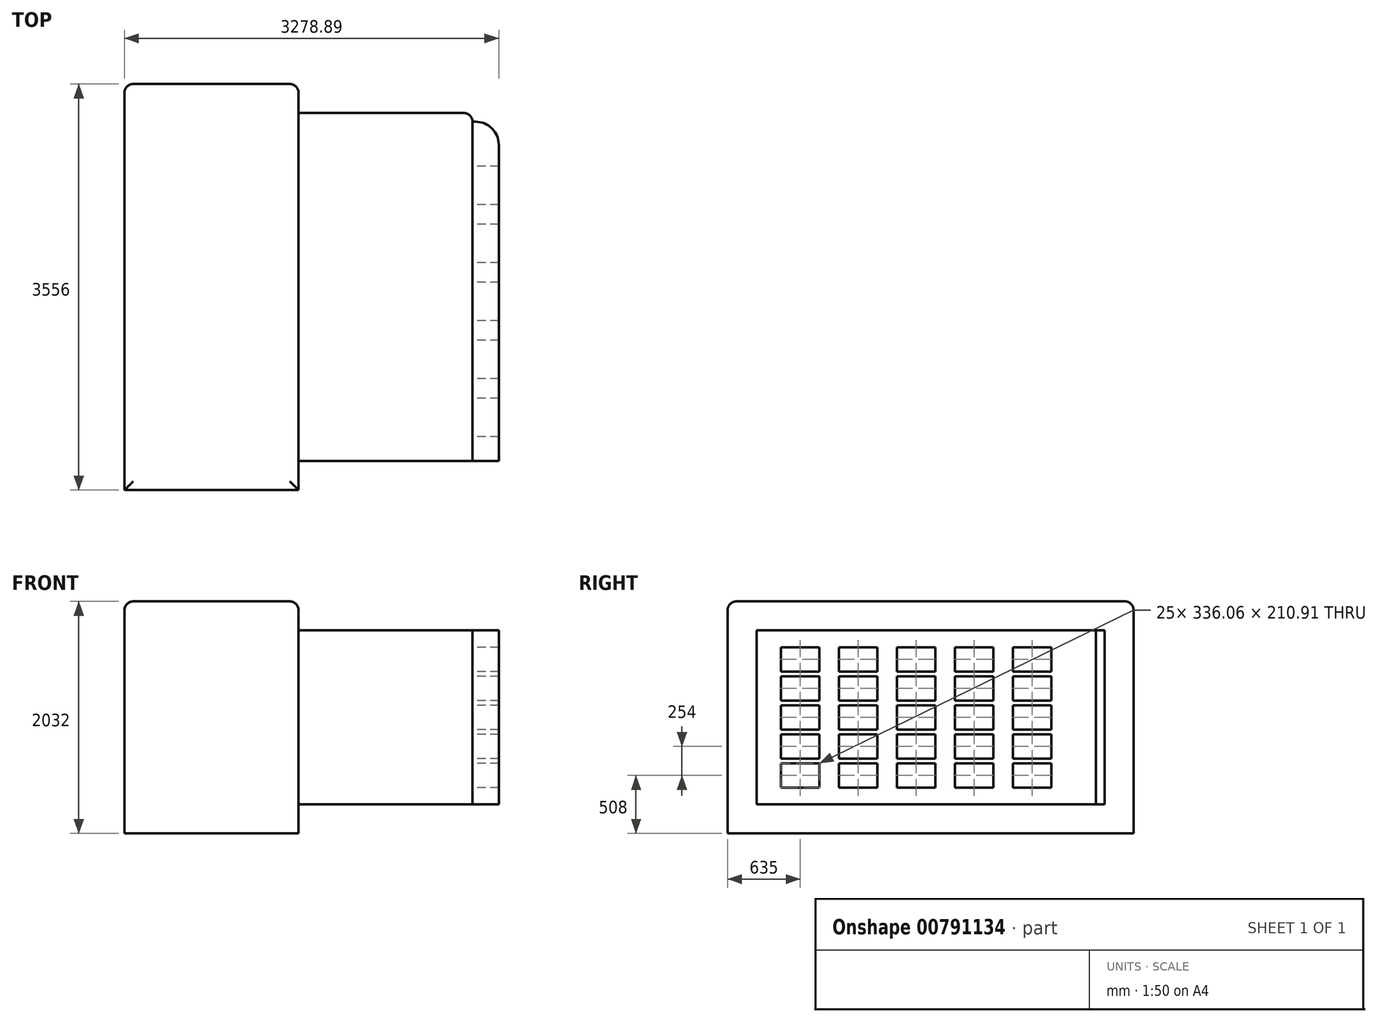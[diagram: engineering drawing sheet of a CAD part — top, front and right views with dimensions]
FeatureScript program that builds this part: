
annotation { "Feature Type Name" : "Feature", "Feature Type Description" : "" }
export const myFeature = defineFeature(function(context is Context, id is Id, definition is map)
    precondition{}
    {
        {
            var Q0;
            Q0=qCreatedBy(makeId("Top.planeOp"),FACE);
            var sketch = newSketch(context, id + "F0", { "sketchPlane" : qUnion([Q0])});
            skLineSegment(sketch, "E0.bottom", {"start": v(1524, -1524) * mm, "end": v(-1524, -1524) * mm});
            skLineSegment(sketch, "E0.top", {"start": v(1524, 1524) * mm, "end": v(-1524, 1524) * mm});
            skLineSegment(sketch, "E0.left", {"start": v(1524, -1524) * mm, "end": v(1524, 1524) * mm});
            skLineSegment(sketch, "E0.right", {"start": v(-1524, -1524) * mm, "end": v(-1524, 1524) * mm});
            skPoint(sketch, "E0.middle", {"position": v(0, 0) * mm});
            skSolve(sketch);
        }
        {
            var Q0;
            Q0 = qSketchRegion(id + "F0", true);
            extrude(context, id + "F1", {"entities" : qUnion([Q0]), "depth" : 1524 * mm, "offsetDistance" : 25.4 * mm});
        }
        {
            var Q0;
            Q0=makeQuery(id+"F1.opExtrude","SWEPT_FACE",FACE,{"disambiguationData":[OSD([sQuery(id+"F0.wireOp",EDGE,"E0.right")])]});
            var sketch = newSketch(context, id + "F2", { "sketchPlane" : qUnion([Q0])});
            skLineSegment(sketch, "E1.0", {"start": v(1524, 1524) * mm, "end": v(-1524, 1524) * mm});
            skLineSegment(sketch, "E2.0", {"start": v(1524, 1524) * mm, "end": v(1524, 0) * mm});
            skLineSegment(sketch, "E3.0", {"start": v(1524, 0) * mm, "end": v(-1524, 0) * mm});
            skLineSegment(sketch, "E4.0", {"start": v(-1524, 1524) * mm, "end": v(-1524, 0) * mm});
            skLineSegment(sketch, "E5.0", {"start": v(1778, 1778) * mm, "end": v(-1778, 1778) * mm});
            skLineSegment(sketch, "E5.1", {"start": v(1778, 1778) * mm, "end": v(1778, -254) * mm});
            skLineSegment(sketch, "E5.2", {"start": v(1778, -254) * mm, "end": v(-1778, -254) * mm});
            skLineSegment(sketch, "E5.3", {"start": v(-1778, 1778) * mm, "end": v(-1778, -254) * mm});
            skSolve(sketch);
        }
        {
            var Q0;
            Q0 = qSketchRegion(id + "F2", true);
            extrude(context, id + "F3", {"entities" : qUnion([Q0]), "operationType" : NewBodyOperationType.ADD, "oppositeDirection" : true, "depth" : 1524 * mm, "offsetDistance" : 25.4 * mm});
        }
        {
            var Q0;
            Q0=makeQuery(id+"F1.opExtrude","SWEPT_EDGE",EDGE,{"disambiguationData":[OSD([sQuery(id+"F0.wireOp",EDGE,"E0.top"),sQuery(id+"F0.wireOp",EDGE,"E0.left")])]});
            var Q1;
            Q1=makeQuery(id+"F3.opExtrude","CAP_EDGE",EDGE,{"disambiguationData":[OSD([sQuery(id+"F2.wireOp",EDGE,"E4.0")])],"isStart":false});
            var Q2;
            Q2=makeQuery(id+"F3.opExtrude","CAP_EDGE",EDGE,{"disambiguationData":[OSD([sQuery(id+"F2.wireOp",EDGE,"E5.3")])],"isStart":false});
            var Q3;
            Q3=makeQuery(id+"F3.opExtrude","CAP_EDGE",EDGE,{"disambiguationData":[OSD([sQuery(id+"F2.wireOp",EDGE,"E5.3")])],"isStart":true});
            var Q4;
            Q4=makeQuery(id+"F3.opExtrude","CAP_EDGE",EDGE,{"disambiguationData":[OSD([sQuery(id+"F2.wireOp",EDGE,"E5.0")])],"isStart":false});
            var Q5;
            Q5=makeQuery(id+"F3.opExtrude","CAP_EDGE",EDGE,{"disambiguationData":[OSD([sQuery(id+"F2.wireOp",EDGE,"E1.0")])],"isStart":false});
            var Q6;
            Q6=makeQuery(id+"F3.opExtrude","SWEPT_FACE",FACE,{"disambiguationData":[OSD([sQuery(id+"F2.wireOp",EDGE,"E5.0")])]});
            fillet(context, id + "F4", {"entities" : qUnion([Q0, Q1, Q2, Q3, Q4, Q5, Q6]), "radius" : 76.2 * mm, "tangentPropagation" : true, "allowEdgeOverflow" : false});
        }
        {
            var Q0;
            Q0=makeQuery(id+"F1.opExtrude","SWEPT_FACE",FACE,{"disambiguationData":[OSD([sQuery(id+"F0.wireOp",EDGE,"E0.left")])]});
            var sketch = newSketch(context, id + "F5", { "sketchPlane" : qUnion([Q0])});
            skLineSegment(sketch, "E6.0", {"start": v(1447.8, 0) * mm, "end": v(1447.8, 1524) * mm});
            skLineSegment(sketch, "E7.0", {"start": v(-1524, 1524) * mm, "end": v(1447.8, 1524) * mm});
            skLineSegment(sketch, "E8.0", {"start": v(-1524, 1524) * mm, "end": v(-1524, 0) * mm});
            skLineSegment(sketch, "E9.0", {"start": v(-1524, 0) * mm, "end": v(1447.8, 0) * mm});
            skLineSegment(sketch, "E10.bottom", {"start": v(-974.97, 359.46) * mm, "end": v(-1311.03, 359.46) * mm});
            skLineSegment(sketch, "E10.top", {"start": v(-974.97, 148.54) * mm, "end": v(-1311.03, 148.54) * mm});
            skLineSegment(sketch, "E10.left", {"start": v(-974.97, 359.46) * mm, "end": v(-974.97, 148.54) * mm});
            skLineSegment(sketch, "E10.right", {"start": v(-1311.03, 359.46) * mm, "end": v(-1311.03, 148.54) * mm});
            skPoint(sketch, "E10.middle", {"position": v(-1143, 254) * mm});
            skLineSegment(sketch, "E11.0.1.0", {"start": v(-1311.03, 613.46) * mm, "end": v(-1311.03, 402.54) * mm});
            skLineSegment(sketch, "E11.0.1.1", {"start": v(-974.97, 613.46) * mm, "end": v(-1311.03, 613.46) * mm});
            skLineSegment(sketch, "E11.0.1.2", {"start": v(-974.97, 613.46) * mm, "end": v(-974.97, 402.54) * mm});
            skLineSegment(sketch, "E11.0.1.3", {"start": v(-974.97, 402.54) * mm, "end": v(-1311.03, 402.54) * mm});
            skLineSegment(sketch, "E11.0.2.0", {"start": v(-1311.03, 867.46) * mm, "end": v(-1311.03, 656.54) * mm});
            skLineSegment(sketch, "E11.0.2.1", {"start": v(-974.97, 867.46) * mm, "end": v(-1311.03, 867.46) * mm});
            skLineSegment(sketch, "E11.0.2.2", {"start": v(-974.97, 867.46) * mm, "end": v(-974.97, 656.54) * mm});
            skLineSegment(sketch, "E11.0.2.3", {"start": v(-974.97, 656.54) * mm, "end": v(-1311.03, 656.54) * mm});
            skLineSegment(sketch, "E11.0.3.0", {"start": v(-1311.03, 1121.46) * mm, "end": v(-1311.03, 910.54) * mm});
            skLineSegment(sketch, "E11.0.3.1", {"start": v(-974.97, 1121.46) * mm, "end": v(-1311.03, 1121.46) * mm});
            skLineSegment(sketch, "E11.0.3.2", {"start": v(-974.97, 1121.46) * mm, "end": v(-974.97, 910.54) * mm});
            skLineSegment(sketch, "E11.0.3.3", {"start": v(-974.97, 910.54) * mm, "end": v(-1311.03, 910.54) * mm});
            skLineSegment(sketch, "E11.0.4.0", {"start": v(-1311.03, 1375.46) * mm, "end": v(-1311.03, 1164.54) * mm});
            skLineSegment(sketch, "E11.0.4.1", {"start": v(-974.97, 1375.46) * mm, "end": v(-1311.03, 1375.46) * mm});
            skLineSegment(sketch, "E11.0.4.2", {"start": v(-974.97, 1375.46) * mm, "end": v(-974.97, 1164.54) * mm});
            skLineSegment(sketch, "E11.0.4.3", {"start": v(-974.97, 1164.54) * mm, "end": v(-1311.03, 1164.54) * mm});
            skLineSegment(sketch, "E11.1.0.0", {"start": v(-803.03, 359.46) * mm, "end": v(-803.03, 148.54) * mm});
            skLineSegment(sketch, "E11.1.0.1", {"start": v(-466.97, 359.46) * mm, "end": v(-803.03, 359.46) * mm});
            skLineSegment(sketch, "E11.1.0.2", {"start": v(-466.97, 359.46) * mm, "end": v(-466.97, 148.54) * mm});
            skLineSegment(sketch, "E11.1.0.3", {"start": v(-466.97, 148.54) * mm, "end": v(-803.03, 148.54) * mm});
            skLineSegment(sketch, "E11.1.1.0", {"start": v(-803.03, 613.46) * mm, "end": v(-803.03, 402.54) * mm});
            skLineSegment(sketch, "E11.1.1.1", {"start": v(-466.97, 613.46) * mm, "end": v(-803.03, 613.46) * mm});
            skLineSegment(sketch, "E11.1.1.2", {"start": v(-466.97, 613.46) * mm, "end": v(-466.97, 402.54) * mm});
            skLineSegment(sketch, "E11.1.1.3", {"start": v(-466.97, 402.54) * mm, "end": v(-803.03, 402.54) * mm});
            skLineSegment(sketch, "E11.1.2.0", {"start": v(-803.03, 867.46) * mm, "end": v(-803.03, 656.54) * mm});
            skLineSegment(sketch, "E11.1.2.1", {"start": v(-466.97, 867.46) * mm, "end": v(-803.03, 867.46) * mm});
            skLineSegment(sketch, "E11.1.2.2", {"start": v(-466.97, 867.46) * mm, "end": v(-466.97, 656.54) * mm});
            skLineSegment(sketch, "E11.1.2.3", {"start": v(-466.97, 656.54) * mm, "end": v(-803.03, 656.54) * mm});
            skLineSegment(sketch, "E11.1.3.0", {"start": v(-803.03, 1121.46) * mm, "end": v(-803.03, 910.54) * mm});
            skLineSegment(sketch, "E11.1.3.1", {"start": v(-466.97, 1121.46) * mm, "end": v(-803.03, 1121.46) * mm});
            skLineSegment(sketch, "E11.1.3.2", {"start": v(-466.97, 1121.46) * mm, "end": v(-466.97, 910.54) * mm});
            skLineSegment(sketch, "E11.1.3.3", {"start": v(-466.97, 910.54) * mm, "end": v(-803.03, 910.54) * mm});
            skLineSegment(sketch, "E11.1.4.0", {"start": v(-803.03, 1375.46) * mm, "end": v(-803.03, 1164.54) * mm});
            skLineSegment(sketch, "E11.1.4.1", {"start": v(-466.97, 1375.46) * mm, "end": v(-803.03, 1375.46) * mm});
            skLineSegment(sketch, "E11.1.4.2", {"start": v(-466.97, 1375.46) * mm, "end": v(-466.97, 1164.54) * mm});
            skLineSegment(sketch, "E11.1.4.3", {"start": v(-466.97, 1164.54) * mm, "end": v(-803.03, 1164.54) * mm});
            skLineSegment(sketch, "E11.2.0.0", {"start": v(-295.03, 359.46) * mm, "end": v(-295.03, 148.54) * mm});
            skLineSegment(sketch, "E11.2.0.1", {"start": v(41.03, 359.46) * mm, "end": v(-295.03, 359.46) * mm});
            skLineSegment(sketch, "E11.2.0.2", {"start": v(41.03, 359.46) * mm, "end": v(41.03, 148.54) * mm});
            skLineSegment(sketch, "E11.2.0.3", {"start": v(41.03, 148.54) * mm, "end": v(-295.03, 148.54) * mm});
            skLineSegment(sketch, "E11.2.1.0", {"start": v(-295.03, 613.46) * mm, "end": v(-295.03, 402.54) * mm});
            skLineSegment(sketch, "E11.2.1.1", {"start": v(41.03, 613.46) * mm, "end": v(-295.03, 613.46) * mm});
            skLineSegment(sketch, "E11.2.1.2", {"start": v(41.03, 613.46) * mm, "end": v(41.03, 402.54) * mm});
            skLineSegment(sketch, "E11.2.1.3", {"start": v(41.03, 402.54) * mm, "end": v(-295.03, 402.54) * mm});
            skLineSegment(sketch, "E11.2.2.0", {"start": v(-295.03, 867.46) * mm, "end": v(-295.03, 656.54) * mm});
            skLineSegment(sketch, "E11.2.2.1", {"start": v(41.03, 867.46) * mm, "end": v(-295.03, 867.46) * mm});
            skLineSegment(sketch, "E11.2.2.2", {"start": v(41.03, 867.46) * mm, "end": v(41.03, 656.54) * mm});
            skLineSegment(sketch, "E11.2.2.3", {"start": v(41.03, 656.54) * mm, "end": v(-295.03, 656.54) * mm});
            skLineSegment(sketch, "E11.2.3.0", {"start": v(-295.03, 1121.46) * mm, "end": v(-295.03, 910.54) * mm});
            skLineSegment(sketch, "E11.2.3.1", {"start": v(41.03, 1121.46) * mm, "end": v(-295.03, 1121.46) * mm});
            skLineSegment(sketch, "E11.2.3.2", {"start": v(41.03, 1121.46) * mm, "end": v(41.03, 910.54) * mm});
            skLineSegment(sketch, "E11.2.3.3", {"start": v(41.03, 910.54) * mm, "end": v(-295.03, 910.54) * mm});
            skLineSegment(sketch, "E11.2.4.0", {"start": v(-295.03, 1375.46) * mm, "end": v(-295.03, 1164.54) * mm});
            skLineSegment(sketch, "E11.2.4.1", {"start": v(41.03, 1375.46) * mm, "end": v(-295.03, 1375.46) * mm});
            skLineSegment(sketch, "E11.2.4.2", {"start": v(41.03, 1375.46) * mm, "end": v(41.03, 1164.54) * mm});
            skLineSegment(sketch, "E11.2.4.3", {"start": v(41.03, 1164.54) * mm, "end": v(-295.03, 1164.54) * mm});
            skLineSegment(sketch, "E11.3.0.0", {"start": v(212.97, 359.46) * mm, "end": v(212.97, 148.54) * mm});
            skLineSegment(sketch, "E11.3.0.1", {"start": v(549.03, 359.46) * mm, "end": v(212.97, 359.46) * mm});
            skLineSegment(sketch, "E11.3.0.2", {"start": v(549.03, 359.46) * mm, "end": v(549.03, 148.54) * mm});
            skLineSegment(sketch, "E11.3.0.3", {"start": v(549.03, 148.54) * mm, "end": v(212.97, 148.54) * mm});
            skLineSegment(sketch, "E11.3.1.0", {"start": v(212.97, 613.46) * mm, "end": v(212.97, 402.54) * mm});
            skLineSegment(sketch, "E11.3.1.1", {"start": v(549.03, 613.46) * mm, "end": v(212.97, 613.46) * mm});
            skLineSegment(sketch, "E11.3.1.2", {"start": v(549.03, 613.46) * mm, "end": v(549.03, 402.54) * mm});
            skLineSegment(sketch, "E11.3.1.3", {"start": v(549.03, 402.54) * mm, "end": v(212.97, 402.54) * mm});
            skLineSegment(sketch, "E11.3.2.0", {"start": v(212.97, 867.46) * mm, "end": v(212.97, 656.54) * mm});
            skLineSegment(sketch, "E11.3.2.1", {"start": v(549.03, 867.46) * mm, "end": v(212.97, 867.46) * mm});
            skLineSegment(sketch, "E11.3.2.2", {"start": v(549.03, 867.46) * mm, "end": v(549.03, 656.54) * mm});
            skLineSegment(sketch, "E11.3.2.3", {"start": v(549.03, 656.54) * mm, "end": v(212.97, 656.54) * mm});
            skLineSegment(sketch, "E11.3.3.0", {"start": v(212.97, 1121.46) * mm, "end": v(212.97, 910.54) * mm});
            skLineSegment(sketch, "E11.3.3.1", {"start": v(549.03, 1121.46) * mm, "end": v(212.97, 1121.46) * mm});
            skLineSegment(sketch, "E11.3.3.2", {"start": v(549.03, 1121.46) * mm, "end": v(549.03, 910.54) * mm});
            skLineSegment(sketch, "E11.3.3.3", {"start": v(549.03, 910.54) * mm, "end": v(212.97, 910.54) * mm});
            skLineSegment(sketch, "E11.3.4.0", {"start": v(212.97, 1375.46) * mm, "end": v(212.97, 1164.54) * mm});
            skLineSegment(sketch, "E11.3.4.1", {"start": v(549.03, 1375.46) * mm, "end": v(212.97, 1375.46) * mm});
            skLineSegment(sketch, "E11.3.4.2", {"start": v(549.03, 1375.46) * mm, "end": v(549.03, 1164.54) * mm});
            skLineSegment(sketch, "E11.3.4.3", {"start": v(549.03, 1164.54) * mm, "end": v(212.97, 1164.54) * mm});
            skLineSegment(sketch, "E11.4.0.0", {"start": v(720.97, 359.46) * mm, "end": v(720.97, 148.54) * mm});
            skLineSegment(sketch, "E11.4.0.1", {"start": v(1057.03, 359.46) * mm, "end": v(720.97, 359.46) * mm});
            skLineSegment(sketch, "E11.4.0.2", {"start": v(1057.03, 359.46) * mm, "end": v(1057.03, 148.54) * mm});
            skLineSegment(sketch, "E11.4.0.3", {"start": v(1057.03, 148.54) * mm, "end": v(720.97, 148.54) * mm});
            skLineSegment(sketch, "E11.4.1.0", {"start": v(720.97, 613.46) * mm, "end": v(720.97, 402.54) * mm});
            skLineSegment(sketch, "E11.4.1.1", {"start": v(1057.03, 613.46) * mm, "end": v(720.97, 613.46) * mm});
            skLineSegment(sketch, "E11.4.1.2", {"start": v(1057.03, 613.46) * mm, "end": v(1057.03, 402.54) * mm});
            skLineSegment(sketch, "E11.4.1.3", {"start": v(1057.03, 402.54) * mm, "end": v(720.97, 402.54) * mm});
            skLineSegment(sketch, "E11.4.2.0", {"start": v(720.97, 867.46) * mm, "end": v(720.97, 656.54) * mm});
            skLineSegment(sketch, "E11.4.2.1", {"start": v(1057.03, 867.46) * mm, "end": v(720.97, 867.46) * mm});
            skLineSegment(sketch, "E11.4.2.2", {"start": v(1057.03, 867.46) * mm, "end": v(1057.03, 656.54) * mm});
            skLineSegment(sketch, "E11.4.2.3", {"start": v(1057.03, 656.54) * mm, "end": v(720.97, 656.54) * mm});
            skLineSegment(sketch, "E11.4.3.0", {"start": v(720.97, 1121.46) * mm, "end": v(720.97, 910.54) * mm});
            skLineSegment(sketch, "E11.4.3.1", {"start": v(1057.03, 1121.46) * mm, "end": v(720.97, 1121.46) * mm});
            skLineSegment(sketch, "E11.4.3.2", {"start": v(1057.03, 1121.46) * mm, "end": v(1057.03, 910.54) * mm});
            skLineSegment(sketch, "E11.4.3.3", {"start": v(1057.03, 910.54) * mm, "end": v(720.97, 910.54) * mm});
            skLineSegment(sketch, "E11.4.4.0", {"start": v(720.97, 1375.46) * mm, "end": v(720.97, 1164.54) * mm});
            skLineSegment(sketch, "E11.4.4.1", {"start": v(1057.03, 1375.46) * mm, "end": v(720.97, 1375.46) * mm});
            skLineSegment(sketch, "E11.4.4.2", {"start": v(1057.03, 1375.46) * mm, "end": v(1057.03, 1164.54) * mm});
            skLineSegment(sketch, "E11.4.4.3", {"start": v(1057.03, 1164.54) * mm, "end": v(720.97, 1164.54) * mm});
            skLineSegment(sketch, "E11.direction1", {"start": v(-1311.03, 148.54) * mm, "end": v(-803.03, 148.54) * mm, "construction": true});
            skLineSegment(sketch, "E11.direction2", {"start": v(-1311.03, 148.54) * mm, "end": v(-1311.03, 402.54) * mm, "construction": true});
            skSolve(sketch);
        }
        {
            var Q0;
            Q0 = qSketchRegion(id + "F5", true);
            extrude(context, id + "F6", {"entities" : qUnion([Q0]), "depth" : 230.89 * mm, "offsetDistance" : 25.4 * mm});
        }
        {
            var Q0;
            Q0=makeQuery(id+"F6.opExtrude","CAP_EDGE",EDGE,{"disambiguationData":[OSD([sQuery(id+"F5.wireOp",EDGE,"E6.0")])],"isStart":false});
            fillet(context, id + "F7", {"entities" : qUnion([Q0]), "radius" : 203.2 * mm, "tangentPropagation" : true, "allowEdgeOverflow" : false});
        }
    });
